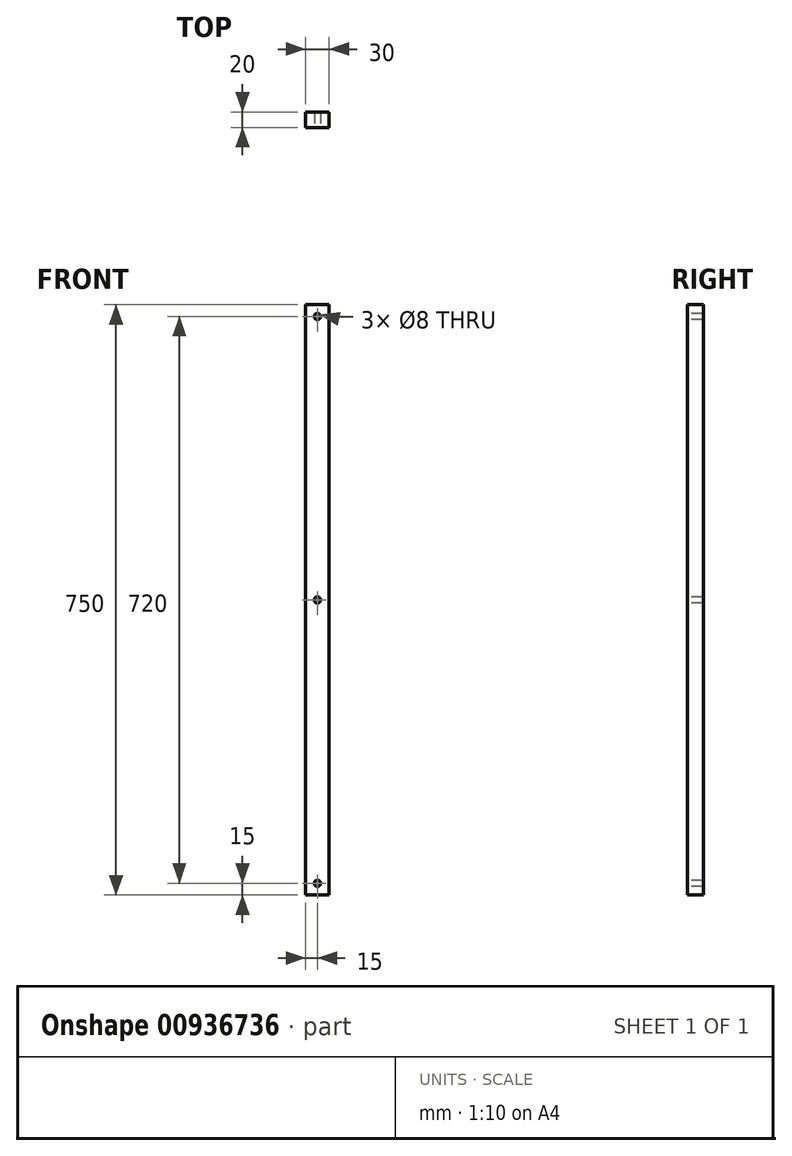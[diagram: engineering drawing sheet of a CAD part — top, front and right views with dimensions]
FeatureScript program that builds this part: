
annotation { "Feature Type Name" : "Feature", "Feature Type Description" : "" }
export const myFeature = defineFeature(function(context is Context, id is Id, definition is map)
    precondition{}
    {
        {
            var Q0;
            Q0=qCreatedBy(makeId("Front.planeOp"),FACE);
            var sketch = newSketch(context, id + "F0", { "sketchPlane" : qUnion([Q0])});
            skLineSegment(sketch, "E0.bottom", {"start": v(15, -375) * mm, "end": v(-15, -375) * mm});
            skLineSegment(sketch, "E0.top", {"start": v(15, 375) * mm, "end": v(-15, 375) * mm});
            skLineSegment(sketch, "E0.left", {"start": v(15, -375) * mm, "end": v(15, 375) * mm});
            skLineSegment(sketch, "E0.right", {"start": v(-15, -375) * mm, "end": v(-15, 375) * mm});
            skPoint(sketch, "E0.middle", {"position": v(0, 0) * mm});
            skSolve(sketch);
        }
        {
            var Q0;
            Q0=makeQuery(id+"F0.imprint","IMPRINT",FACE,{"disambiguationData":[TD([[makeQuery(id+"F0.imprint","IMPRINT",EDGE,{"derivedFrom":sQuery(id+"F0.wireOp",EDGE,"E0.bottom")}),-1.0]])]});
            extrude(context, id + "F1", {"entities" : qUnion([Q0]), "depth" : 20 * mm, "offsetDistance" : 25 * mm});
        }
        {
            var Q0;
            Q0=makeQuery(id+"F1.opExtrude","CAP_FACE",FACE,{"disambiguationData":[OSD([sQuery(id+"F0.wireOp",EDGE,"E0.bottom"),sQuery(id+"F0.wireOp",EDGE,"E0.top"),sQuery(id+"F0.wireOp",EDGE,"E0.left"),sQuery(id+"F0.wireOp",EDGE,"E0.right")])],"isStart":false});
            var sketch = newSketch(context, id + "F2", { "sketchPlane" : qUnion([Q0])});
            skCircle(sketch, "E1", {"center": v(0, -360) * mm, "radius": 4 * mm});
            skCircle(sketch, "E2", {"center": v(0, 360) * mm, "radius": 4 * mm});
            skSolve(sketch);
        }
        {
            var Q0;
            Q0=sQuery(id+"F2.wireOp",VERTEX,"E2.center");
            var Q1;
            Q1=sQuery(id+"F2.wireOp",VERTEX,"E1.center");
            var Q2;
            Q2=makeQuery(id+"F1.opExtrude","SWEPT_BODY",BODY,{"disambiguationData":[OSD([sQuery(id+"F0.wireOp",EDGE,"E0.bottom"),sQuery(id+"F0.wireOp",EDGE,"E0.top"),sQuery(id+"F0.wireOp",EDGE,"E0.left"),sQuery(id+"F0.wireOp",EDGE,"E0.right")])]});
            hole(context, id + "F3", {"style" : HoleStyle.SIMPLE, "endStyle" : HoleEndStyle.THROUGH, "holeDiameter" : 8 * mm, "majorDiameter" : 5 * mm, "isTappedThrough" : true, "tappedDepth" : 12 * mm, "tapClearance" : 3, "locations" : qUnion([Q0, Q1]), "scope" : qUnion([Q2])});
        }
        {
            var Q0;
            Q0=makeQuery(id+"F1.opExtrude","CAP_FACE",FACE,{"disambiguationData":[OSD([sQuery(id+"F0.wireOp",EDGE,"E0.bottom"),sQuery(id+"F0.wireOp",EDGE,"E0.top"),sQuery(id+"F0.wireOp",EDGE,"E0.left"),sQuery(id+"F0.wireOp",EDGE,"E0.right")])],"isStart":false});
            var sketch = newSketch(context, id + "F4", { "sketchPlane" : qUnion([Q0])});
            skCircle(sketch, "E3", {"center": v(0, 0) * mm, "radius": 4 * mm});
            skSolve(sketch);
        }
        {
            var Q0;
            Q0=sQuery(id+"F4.wireOp",VERTEX,"E3.center");
            var Q1;
            Q1=makeQuery(id+"F1.opExtrude","SWEPT_BODY",BODY,{"disambiguationData":[OSD([sQuery(id+"F0.wireOp",EDGE,"E0.bottom"),sQuery(id+"F0.wireOp",EDGE,"E0.top"),sQuery(id+"F0.wireOp",EDGE,"E0.left"),sQuery(id+"F0.wireOp",EDGE,"E0.right")])]});
            hole(context, id + "F5", {"style" : HoleStyle.SIMPLE, "endStyle" : HoleEndStyle.THROUGH, "holeDiameter" : 8 * mm, "majorDiameter" : 5 * mm, "isTappedThrough" : true, "tappedDepth" : 12 * mm, "tapClearance" : 3, "locations" : qUnion([Q0]), "scope" : qUnion([Q1])});
        }
    });
